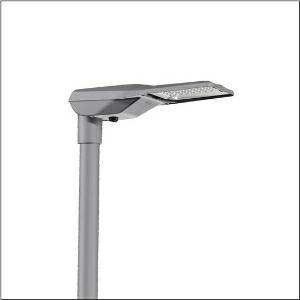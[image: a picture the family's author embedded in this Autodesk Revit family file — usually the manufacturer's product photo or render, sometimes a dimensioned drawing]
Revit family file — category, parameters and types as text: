
# Revit family: streetlight_sl_21_iq_mini___st1_0a_5xe2d31u08jb_b0df
name_source: partatom
category: Lighting Fixtures
units: mm (PartAtom-declared; Revit-internal decimal feet)

## family parameters
Cut with Voids When Loaded = No
Host = Face
Light Source = No
Part Type = Normal
Room Calculation Point = No
Round Connector Dimension = Use Diameter
Shared = No

## types (1)
- --- (1 x LED, 11210 lm, 72.5 W, 3000K)
    Apparent Load = 73 VA
    CIE Flux Codes = 40 73 97 100 100
    Color Rendering = 70
    Color Temperature = 3000K
    Default Elevation = 1800 mm
    Description = Streetlight SL 21 iQ mini, mast luminaire, primary light control with lens, of PMMA, primary optical cover: cover, of toughened safety glass, transparent, light distribution: ST1.0a, light emission: direct distribution, primary light characteristic: asymmetric, installation type: post-top, side-entry, LED, High Power LED, rated luminous flux: 11.210lm, luminous efficacy: 155lm/W, light colour: 730, colour temperature: 3000K, control gear: iQ-Street Remote, D4i with power reduction, control: pre-setting: logarithmic dimming characteristic, Street-Remote, Auto-Match, Temp-Guard, Lumen-Switch, Night-Set, Smart-Wire, Light-Fading, Desk-Remote (wireless, voltage-free reading and setting of iQ features in the workshop via application-optimized NFC function/RFID function), optimised constant luminous flux control (CLO 2.0), mains connection: 220..240V, AC, 50/60Hz, start of lifetime: 73W, end of service life: 76W, reduction: 33W, luminaire housing, of diecast aluminium, powder-coated, SITECO metallic grey (DB 702S), corrosivity category C5 high according to DIN EN ISO 12944, please order mast flange separately, inclination adjustable: 0°, 5°, 10°, 15°, sealing non-destructively replaceable, multi-level sealing system, length: 628mm, width: 235mm, height: 110mm, mast flange for spigot size: 42mm (side-entry): 5XC10008XM4, 60/48mm (side-entry/post-top): 5XC10108XM2, 76/60mm (side-entry/post-top): 5XC10108XM1, mounting height: 4..8m, Smart Interface below, protection rating (complete): IP66, insulation class (complete): insulation class II (safety insulation), certification: CE, ENEC, ENEC+, VDE, impact resistance: IK10, permissible operating ambient temperature for outdoor applications: -40..+50°C, standard-compliant lighting for roads and squares, packaging unit: 1 piece

Light Distribution: ST1.0a
    Height = 110 mm
    Lamp = 1 x LED
    Lamp Light Flux = 11210 lm
    Lamp Power = 72.5 W
    Lamp count = 1
    Length = 625 mm
    Luminous efficacy = 155 lm/W
    Manufacturer = Siteco
    ModVariant = No
    Model = 5XE2D31U08JB
    Number of Poles = 1
    OnlyDefault = Yes
    Power Factor = 1
    Product Name = Streetlight SL 21 iQ mini | ST1.0a
    Product group = mast luminaire | pylon top
    ProductGroupID = 6100
    Protection Class = Protection class II
    Protection Degree = IP 66
    RLX_Detail_Level = 1
    RLX_Emergency_Light_Flux = 0 lm
    RLX_Emergency_Type = 0
    RLX_Emergency_Type_DB = No
    RlxData = <blob elided: 94221 chars, md5=f08a2e49>
    Socket = socket
    Standby Power = 0 W
    System Light Flux = 11210 lm
    System Power = 73 W
    Type Comments = factory setting: luminous flux: 100 % | dim-lin: 254 | 755 mA
    Type Image = l_1003516.jpg
    URL = http://relux.com
    VarID = @adj_114347
    Voltage = 0 V
    Weight = 0.00 kg
    Width = 234 mm

## geometry (parser evidence)
native form markers: Blend x4, Sweep x9
no freeform markers — native parametric forms only
